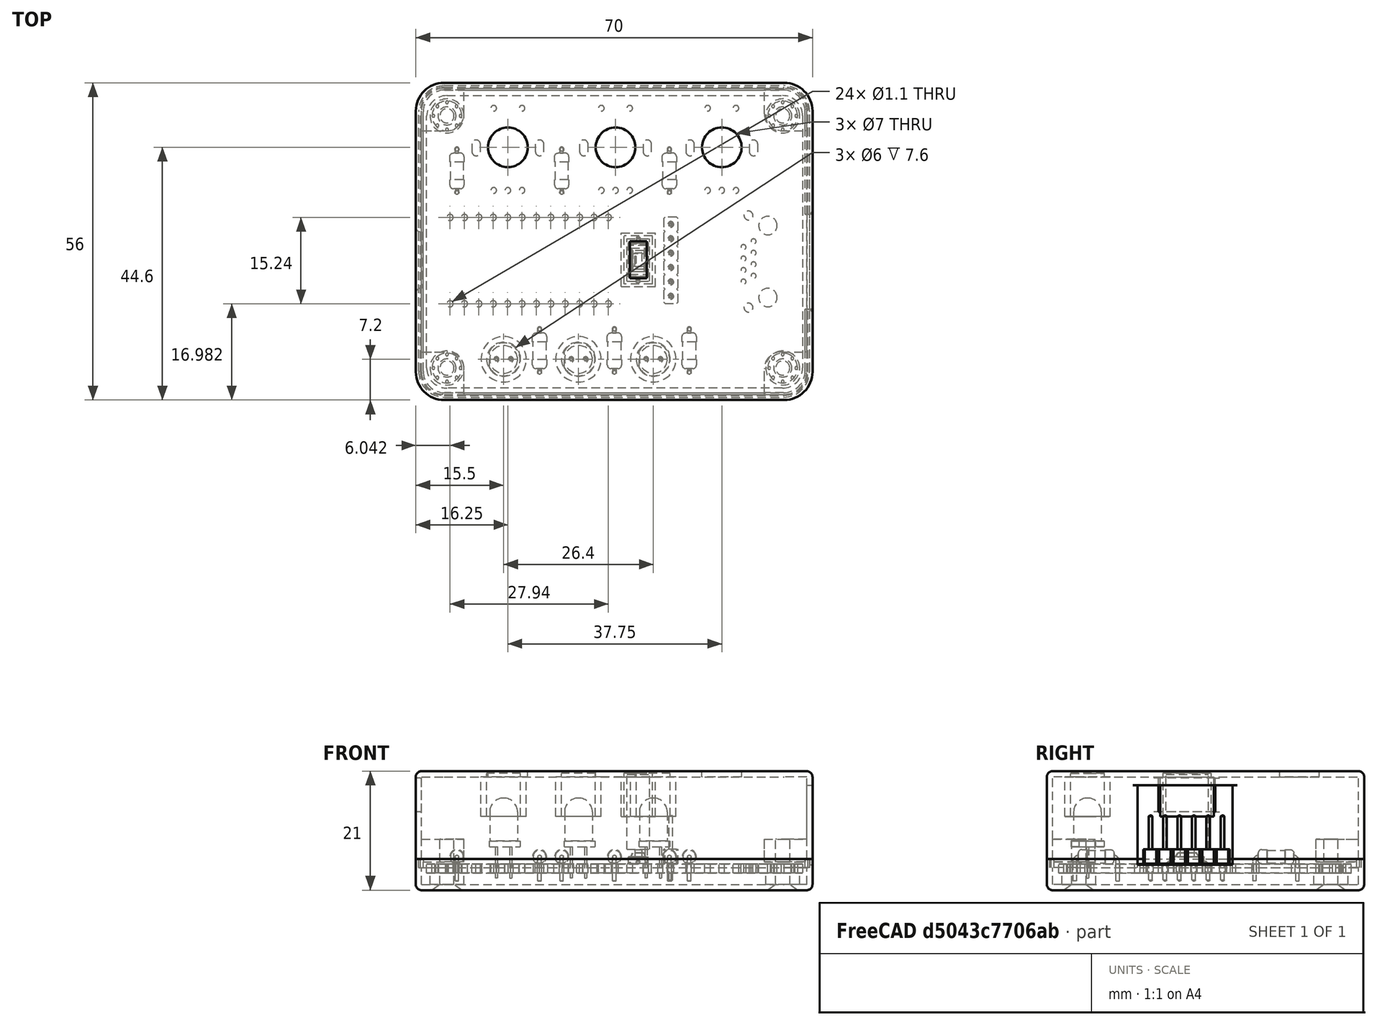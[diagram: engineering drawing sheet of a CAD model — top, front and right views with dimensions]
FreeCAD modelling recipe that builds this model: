
FCSTD DOCUMENT  (FreeCAD 0.19R24276 (Git))
Label: case
License: All rights reserved
LicenseURL: http://en.wikipedia.org/wiki/All_rights_reserved
objects: Part::Cylinder×21, Part::Box×16, Part::Fillet×10, Part::MultiFuse×6, Mesh::Feature×4, Part::Cone×4, Part::Cut×3, Part::Thickness×2, Part::Feature×1
note: 63 computed .brp shape members not serialized (recipe doc carries the construction recipe); baked Part::Feature solids carry a one-line shape summary decoded from their .brp

FEATURE [Part::Feature] Feature  label="modelMterminalAdapter"
  Placement = pos=(-55,106,2) rot=(0,0,1;0rad)
  shape: bbox 66.35 x 51.63 x 14.6 mm, 540 faces, 12 solids (baked)
FEATURE [Part::Box] Box  label="Cube"
  AttacherType = Attacher::AttachEngine3D
  Height = 4.5
  Length = 68
  Width = 54
FEATURE [Part::Box] Box001  label="rj45hole"
  AttacherType = Attacher::AttachEngine3D
  Height = 14.5
  Length = 24
  Placement = pos=(47,15,3) rot=(0,0,1;0rad)
  Width = 16.8
FEATURE [Part::Cylinder] Cylinder  label="PotHole"
  Angle = 360
  AttacherType = Attacher::AttachEngine3D
  Height = 10
  Placement = pos=(15.25,43.6,11) rot=(0,0,1;0rad)
  Radius = 3.5
FEATURE [Part::Cylinder] Cylinder001  label="PotHole001"
  Angle = 360
  AttacherType = Attacher::AttachEngine3D
  Height = 10
  Placement = pos=(34.25,43.6,11) rot=(0,0,1;0rad)
  Radius = 3.5
FEATURE [Part::Cylinder] Cylinder002  label="PotHole002"
  Angle = 360
  AttacherType = Attacher::AttachEngine3D
  Height = 10
  Placement = pos=(53,43.6,11) rot=(0,0,1;0rad)
  Radius = 3.5
FEATURE [Mesh::Feature] Arduino_Pro_Micro_Header
  Placement = pos=(-8.9,7.6,5) rot=(0,0,1;0rad)
FEATURE [Part::Cylinder] Cylinder003  label="holebl"
  Angle = 360
  AttacherType = Attacher::AttachEngine3D
  Height = 4
  Placement = pos=(4.5,4.65,-2) rot=(0,0,1;0rad)
  Radius = 1.25
FEATURE [Part::Cylinder] Cylinder004  label="supportbl"
  Angle = 360
  AttacherType = Attacher::AttachEngine3D
  Height = 3
  Placement = pos=(4.5,4.65,-1) rot=(0,0,1;0rad)
  Radius = 3
FEATURE [Part::Cylinder] Cylinder005  label="holetl"
  Angle = 360
  AttacherType = Attacher::AttachEngine3D
  Height = 4
  Placement = pos=(4.5,49.15,-2) rot=(0,0,1;0rad)
  Radius = 1.25
FEATURE [Part::Cylinder] Cylinder006  label="supporttl"
  Angle = 360
  AttacherType = Attacher::AttachEngine3D
  Height = 3
  Placement = pos=(4.5,49.15,-1) rot=(0,0,1;0rad)
  Radius = 3
FEATURE [Part::Cylinder] Cylinder007  label="holebr"
  Angle = 360
  AttacherType = Attacher::AttachEngine3D
  Height = 4
  Placement = pos=(63.75,4.65,-2) rot=(0,0,1;0rad)
  Radius = 1.25
FEATURE [Part::Cylinder] Cylinder008  label="supportbr"
  Angle = 360
  AttacherType = Attacher::AttachEngine3D
  Height = 3
  Placement = pos=(63.75,4.65,-1) rot=(0,0,1;0rad)
  Radius = 3
FEATURE [Part::Cylinder] Cylinder009  label="holetr"
  Angle = 360
  AttacherType = Attacher::AttachEngine3D
  Height = 4
  Placement = pos=(63.75,49.15,-2) rot=(0,0,1;0rad)
  Radius = 1.25
FEATURE [Part::Cylinder] Cylinder010  label="supporttr"
  Angle = 360
  AttacherType = Attacher::AttachEngine3D
  Height = 3
  Placement = pos=(63.75,49.15,-1) rot=(0,0,1;0rad)
  Radius = 3
FEATURE [Part::Box] Box002  label="Cube002"
  AttacherType = Attacher::AttachEngine3D
  Height = 14.5
  Length = 68
  Placement = pos=(0,0,4.5) rot=(0,0,1;0rad)
  Width = 54
FEATURE [Part::Box] Box003  label="UsbHole"
  AttacherType = Attacher::AttachEngine3D
  Height = 6
  Length = 10
  Placement = pos=(-3,18.7,12.8) rot=(0,0,1;0rad)
  Width = 10
FEATURE [Part::Cylinder] Cylinder011  label="ledhole"
  Angle = 360
  AttacherType = Attacher::AttachEngine3D
  Height = 7.6
  Placement = pos=(14.5,6.2,12) rot=(0,0,1;0rad)
  Radius = 3
FEATURE [Part::Cylinder] Cylinder012  label="ledtube"
  Angle = 360
  AttacherType = Attacher::AttachEngine3D
  Height = 7
  Placement = pos=(14.5,6.2,12) rot=(0,0,1;0rad)
  Radius = 4
FEATURE [Part::Cylinder] Cylinder013  label="ledhole001"
  Angle = 360
  AttacherType = Attacher::AttachEngine3D
  Height = 7.6
  Placement = pos=(27.7,6.2,12) rot=(0,0,1;0rad)
  Radius = 3
FEATURE [Part::Cylinder] Cylinder014  label="ledtube001"
  Angle = 360
  AttacherType = Attacher::AttachEngine3D
  Height = 7
  Placement = pos=(27.7,6.2,12) rot=(0,0,1;0rad)
  Radius = 4
FEATURE [Part::Cylinder] Cylinder015  label="ledhole002"
  Angle = 360
  AttacherType = Attacher::AttachEngine3D
  Height = 7.6
  Placement = pos=(40.9,6.2,12) rot=(0,0,1;0rad)
  Radius = 3
FEATURE [Part::Cylinder] Cylinder016  label="ledtube002"
  Angle = 360
  AttacherType = Attacher::AttachEngine3D
  Height = 7
  Placement = pos=(40.9,6.2,12) rot=(0,0,1;0rad)
  Radius = 4
FEATURE [Part::Box] Box004  label="ResetHousing"
  AttacherType = Attacher::AttachEngine3D
  Height = 7
  Length = 6
  Placement = pos=(35.25,19,12) rot=(0,0,1;0rad)
  Width = 9.5
FEATURE [Part::Box] Box005  label="ResetHole"
  AttacherType = Attacher::AttachEngine3D
  Height = 13.5
  Length = 5
  Placement = pos=(35.75,19.5,6.2) rot=(0,0,1;0rad)
  Width = 8.5
FEATURE [Part::Box] Box006  label="ResetHole001"
  AttacherType = Attacher::AttachEngine3D
  Height = 14.5
  Length = 3
  Placement = pos=(36.75,20.5,6.2) rot=(0,0,1;0rad)
  Width = 6.5
FEATURE [Part::Box] Box007  label="ResetButton"
  AttacherType = Attacher::AttachEngine3D
  Height = 13.2
  Length = 4
  Placement = pos=(36.25,20,6.2) rot=(0,0,1;0rad)
  Width = 7.5
FEATURE [Part::MultiFuse] Fusion  label="ResetHole002"
  Shapes = -> [Box006,Box005]
FEATURE [Part::Cylinder] Cylinder017  label="holebl001"
  Angle = 360
  AttacherType = Attacher::AttachEngine3D
  Height = 10
  Placement = pos=(4.5,4.65,-2) rot=(0,0,1;0rad)
  Radius = 1.25
FEATURE [Part::Box] Box008  label="Cube004"
  AttacherType = Attacher::AttachEngine3D
  Height = 4
  Length = 7.5
  Placement = pos=(0,0,4) rot=(0,0,1;0rad)
  Width = 7.5
FEATURE [Part::Fillet] Fillet  label="topholebl"
  Base = -> Box008
  Edges = 2 edges: [Edge1 r=4,Edge7 r=3]
FEATURE [Part::Box] Box009  label="Cube005"
  AttacherType = Attacher::AttachEngine3D
  Height = 4
  Length = 7.5
  Placement = pos=(0,0,4) rot=(0,0,1;0rad)
  Width = 7.5
FEATURE [Part::Fillet] Fillet001  label="topholetl"
  Base = -> Box009
  Edges = 2 edges: [Edge3 r=4,Edge5 r=3]
  Placement = pos=(0,46.5,0) rot=(0,0,1;0rad)
FEATURE [Part::Box] Box010  label="Cube006"
  AttacherType = Attacher::AttachEngine3D
  Height = 4
  Length = 7.5
  Placement = pos=(0,0,4) rot=(0,0,1;0rad)
  Width = 7.5
FEATURE [Part::Fillet] Fillet002  label="topholebr"
  Base = -> Box010
  Edges = 2 edges: [Edge3 r=3,Edge5 r=4]
  Placement = pos=(60.5,0,0) rot=(0,0,1;0rad)
FEATURE [Part::Box] Box011  label="Cube007"
  AttacherType = Attacher::AttachEngine3D
  Height = 4
  Length = 7.5
  Placement = pos=(0,0,4) rot=(0,0,1;0rad)
  Width = 7.5
FEATURE [Part::Cylinder] Cylinder018  label="holebl002"
  Angle = 360
  AttacherType = Attacher::AttachEngine3D
  Height = 10
  Placement = pos=(4.5,49.15,-2) rot=(0,0,1;0rad)
  Radius = 1.25
FEATURE [Part::Cylinder] Cylinder019  label="holebl003"
  Angle = 360
  AttacherType = Attacher::AttachEngine3D
  Height = 10
  Placement = pos=(63.75,49.15,-2) rot=(0,0,1;0rad)
  Radius = 1.25
FEATURE [Part::Cylinder] Cylinder020  label="holebl004"
  Angle = 360
  AttacherType = Attacher::AttachEngine3D
  Height = 10
  Placement = pos=(63.75,4.65,-2) rot=(0,0,1;0rad)
  Radius = 1.25
FEATURE [Part::Box] Box012  label="snapbottom"
  AttacherType = Attacher::AttachEngine3D
  Height = 1.5
  Length = 69
  Placement = pos=(-0.5,-0.5,3) rot=(0,0,1;0rad)
  Width = 55
FEATURE [Part::Fillet] Fillet004  label="snapbottom001"
  Base = -> Box012
  Edges = 4 edges r=4.6: [Edge1,Edge3,Edge5,Edge7]
FEATURE [Part::Box] Box013  label="snaptop001"
  AttacherType = Attacher::AttachEngine3D
  Height = 1.5
  Length = 68.4
  Placement = pos=(-0.2,-0.2,3) rot=(0,0,1;0rad)
  Width = 54.4
FEATURE [Part::Cone] Cone  label="ScrewCone"
  Angle = 360
  AttacherType = Attacher::AttachEngine3D
  Height = 2
  Placement = pos=(4.5,4.65,-2) rot=(0,0,1;0rad)
  Radius1 = 4
  Radius2 = 1.25
FEATURE [Part::Cone] Cone001  label="ScrewCone001"
  Angle = 360
  AttacherType = Attacher::AttachEngine3D
  Height = 2
  Placement = pos=(4.5,49.15,-2) rot=(0,0,1;0rad)
  Radius1 = 4
  Radius2 = 1.25
FEATURE [Part::Cone] Cone002  label="ScrewCone002"
  Angle = 360
  AttacherType = Attacher::AttachEngine3D
  Height = 2
  Placement = pos=(63.75,49.15,-2) rot=(0,0,1;0rad)
  Radius1 = 4
  Radius2 = 1.25
FEATURE [Part::Cone] Cone003  label="ScrewCone003"
  Angle = 360
  AttacherType = Attacher::AttachEngine3D
  Height = 2
  Placement = pos=(63.75,4.65,-2) rot=(0,0,1;0rad)
  Radius1 = 4
  Radius2 = 1.25
FEATURE [Part::MultiFuse] Fusion001  label="BottomScrewHoles"
  Shapes = -> [Cone,Cone001,Cone002,Cone003,Cylinder005,Cylinder007,Cylinder009,Cylinder003]
FEATURE [Part::Box] Box015  label="rj45hole001"
  AttacherType = Attacher::AttachEngine3D
  Height = 18
  Length = 24
  Placement = pos=(47,15,3.5) rot=(0,0,1;0rad)
  Width = 16.8
FEATURE [Part::Fillet] Fillet006
  Base = -> Box
  Edges = 4 edges r=4: [Edge1,Edge3,Edge5,Edge7]
FEATURE [Part::Thickness] Thickness
  Faces = -> Fillet006 [Face2]
  Intersection = false
  Join = 0
  Mode = 0
  SelfIntersection = false
  Value = 1
FEATURE [Part::MultiFuse] Fusion006  label="BottomSolid"
  Shapes = -> [Cylinder004,Cylinder006,Cylinder008,Cylinder010,Thickness]
FEATURE [Part::MultiFuse] Fusion007  label="BottomHoles"
  Shapes = -> [Box015,Fillet004,Fusion001]
FEATURE [Part::Cut] Cut003  label="Bottom"
  Base = -> Fusion006
  Tool = -> Fusion007
FEATURE [Part::Fillet] Fillet007
  Base = -> Box002
  Edges = 4 edges r=4: [Edge1,Edge3,Edge5,Edge7]
FEATURE [Part::Thickness] Thickness001
  Faces = -> Fillet007 [Face5]
  Intersection = false
  Join = 0
  Mode = 0
  SelfIntersection = false
  Value = 1
FEATURE [Part::Fillet] Fillet003  label="topholetr"
  Base = -> Box011
  Edges = 2 edges: [Edge1 r=3,Edge7 r=4]
  Placement = pos=(60.5,46.5,0) rot=(0,0,1;0rad)
FEATURE [Part::MultiFuse] Fusion009  label="TopHoles"
  Shapes = -> [Cylinder020,Cylinder019,Cylinder018,Cylinder017,Fusion,Cylinder015,Cylinder013,Cylinder011,Box003,Cylinder002,Cylinder001,Cylinder,Box001]
FEATURE [Mesh::Feature] Mesh  label="Bottom (Meshed)"
  Placement = pos=(0,-70,0) rot=(0,0,1;0rad)
FEATURE [Part::Fillet] Fillet008
  Base = -> Box013
  Edges = 4 edges r=4.2: [Edge1,Edge3,Edge5,Edge7]
FEATURE [Part::Box] Box016  label="snaptop002"
  AttacherType = Attacher::AttachEngine3D
  Height = 1.5
  Length = 67.4
  Placement = pos=(0.3,0.3,3) rot=(0,0,1;0rad)
  Width = 53.4
FEATURE [Part::Fillet] Fillet009
  Base = -> Box016
  Edges = 4 edges r=3.8: [Edge1,Edge3,Edge5,Edge7]
FEATURE [Part::Cut] Cut  label="snaptop"
  Base = -> Fillet008
  Tool = -> Fillet009
FEATURE [Part::MultiFuse] Fusion008  label="TopSolid"
  Shapes = -> [Thickness001,Fillet003,Fillet002,Fillet001,Cylinder,Box004,Cylinder012,Cylinder014,Cylinder016,Fillet,Cut]
FEATURE [Part::Cut] Cut004  label="Top1"
  Base = -> Fusion008
  Tool = -> Fusion009
FEATURE [Part::Fillet] Fillet010  label="Top"
  Base = -> Cut004
  Edges = 9 edges: [Edge52 r=0.2,Edge57 r=0.8,Edge60 r=0.8,Edge131 r=0.2,Edge141 r=0.2,Edge153 r=0.2,Edge158 r=0.8,Edge166 r=0.8,Edge169 r=0.2]
FEATURE [Mesh::Feature] Mesh001  label="Top (Meshed)"
  Placement = pos=(145,0,0) rot=(0,-1,0;3.14159rad)
FEATURE [Mesh::Feature] Mesh002  label="ResetButton (Meshed)"
  Placement = pos=(46,-23,0) rot=(0,1,0;1.5708rad)
